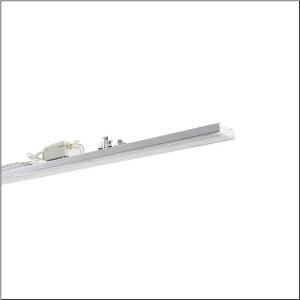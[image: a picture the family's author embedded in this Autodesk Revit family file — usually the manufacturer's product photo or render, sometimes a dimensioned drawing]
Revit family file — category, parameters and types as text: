
# Revit family: licross_11_recessed_ho_51te12cn4c5m
name_source: partatom
category: Lighting Fixtures
units: mm (PartAtom-declared; Revit-internal decimal feet)

## family parameters
Cut with Voids When Loaded = No
Host = Face
Light Source = No
Part Type = Normal
Room Calculation Point = No
Round Connector Dimension = Use Diameter
Shared = No

## types (1)
- --- (1 x LED, 12740 lm, 66.5 W, 4000K)
    Apparent Load = 67 VA
    CIE Flux Codes = 66 91 98 100 100
    Color Rendering = 80
    Color Temperature = 4000K
    Default Elevation = 1800 mm
    Description = Licross 11 Recessed HO, luminaire insert, of sheet steel, galvanised, coil coated, white, length: 1.500mm, width: 66mm, height: 67mm, LED rated luminous flux: 12.740lm, light colour: 840, SDCM (Standard Deviation of Colour Matching)MacAdam ≤ 2 SDCM (initial), control gear: ON/OFF Multilumen, CLOi, with plug, 3-pole, with phase selection, mains connection: 220..240V, AC, 50/60Hz, start of lifetime: 67W, end of service life: 75W, internal wiring halogen-free, primary optical cover: cover, of PMMA, light emission: direct distribution, primary light characteristic: symmetric, protection rating (complete): IP54, insulation class (complete): insulation class I (protective earthing), certification: CE, ENEC, VDE, UKCA, protection symbol: D if used in an environment with non-conductive dust loads with corresponding accessories, impact resistance: IK06, permissible ambient temperature for indoor applications: -35..+35°C, corresponds to IFS (International Featured Standards) requirements for safety and quality in the food industry, reducing of maximum allowable ambient temperature of 5°C with ceiling mounting, LABS conformity tested according to VDMA 24364:2018-05, The light source and the operating device comply with the requirements of the Ecodesign Regulation (EU) 2019/2020 and are replaceable in accordance with this regulation, packaging unit: 1 piece
    Height = 58 mm
    Lamp = 1 x LED
    Lamp Light Flux = 12740 lm
    Lamp Power = 66.5 W
    Lamp count = 1
    Length = 1500 mm
    Luminous efficacy = 192 lm/W
    Manufacturer = Siteco
    ModVariant = No
    Model = 51TE12CN4C5M
    Mounting Place = Ceiling
    Mounting Type = Pendant
    Number of Poles = 1
    OnlyDefault = Yes
    Power Factor = 1
    Product Name = Licross 11 Recessed HO
    Product group = luminaire insert | ceiling pendant
    ProductGroupID = 901
    Protection Class = Protection class I
    Protection Degree = IP 54
    RLX_Detail_Level = 1
    RLX_Emergency_Light_Flux = 0 lm
    RLX_Emergency_Type = 0
    RLX_Emergency_Type_DB = No
    RlxData = <blob elided: 22513 chars, md5=db5e145f>
    Socket = socket
    Standby Power = 0 W
    System Light Flux = 12740 lm
    System Power = 67 W
    Type Comments = factory setting: luminous flux: 100 % | (A | C | E) | 156 mA
    Type Image = l_1296930.jpg
    URL = http://relux.com
    VarID = @adj_000289
    Voltage = 0 V
    Weight = 0.00 kg
    Width = 66 mm

## geometry (parser evidence)
native form markers: Blend x4, Sweep x10
no freeform markers — native parametric forms only
